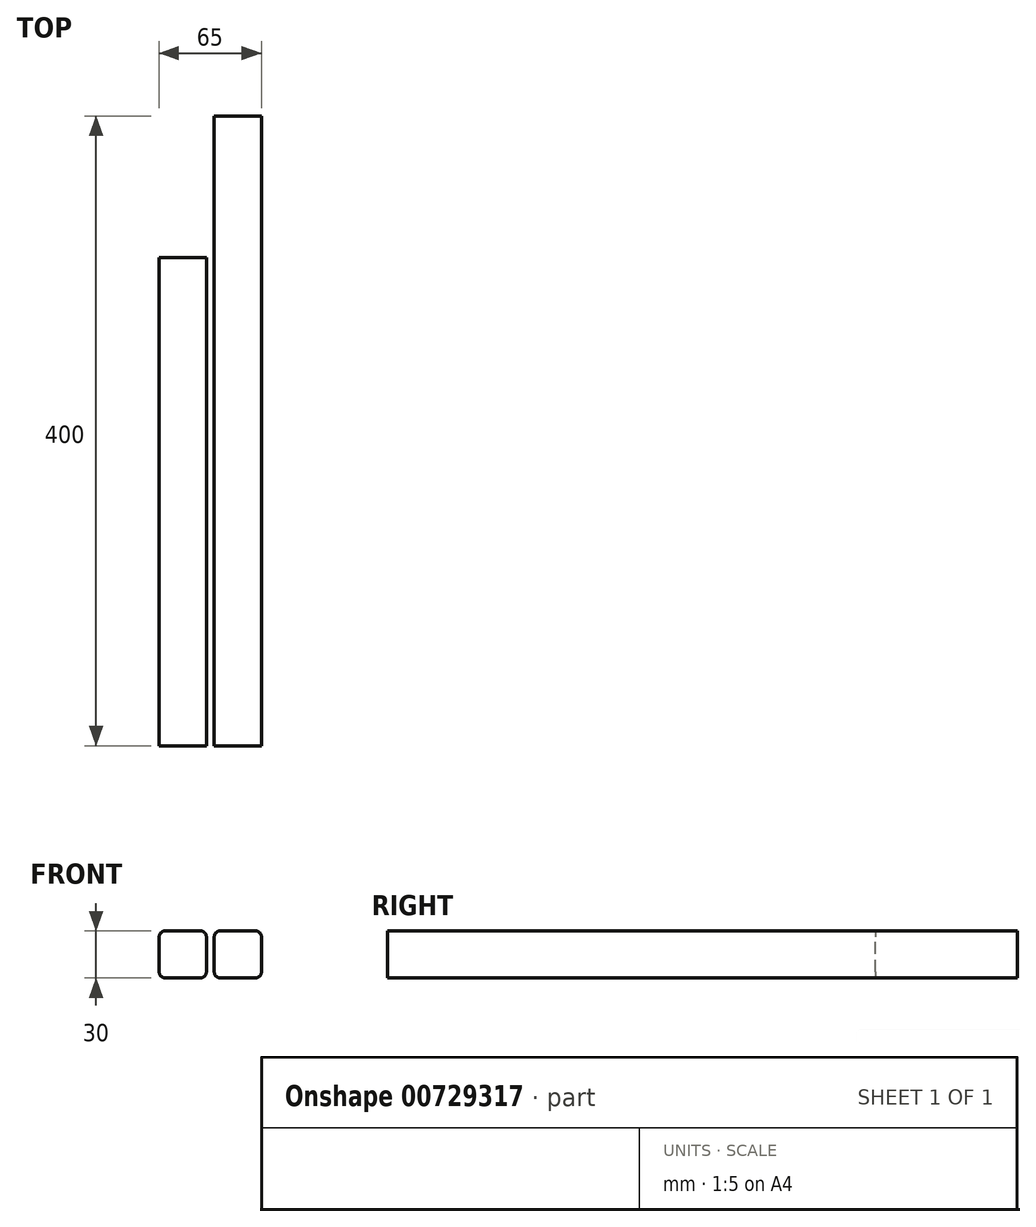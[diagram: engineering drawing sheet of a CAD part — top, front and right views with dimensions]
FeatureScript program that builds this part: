
annotation { "Feature Type Name" : "Feature", "Feature Type Description" : "" }
export const myFeature = defineFeature(function(context is Context, id is Id, definition is map)
    precondition{}
    {
        {
            var Q0;
            Q0=qCreatedBy(makeId("Front.planeOp"),FACE);
            var sketch = newSketch(context, id + "F0", { "sketchPlane" : qUnion([Q0])});
            skLineSegment(sketch, "E0.bottom", {"start": v(0, 0) * mm, "end": v(30, 0) * mm});
            skLineSegment(sketch, "E0.top", {"start": v(0, 30) * mm, "end": v(30, 30) * mm});
            skLineSegment(sketch, "E0.left", {"start": v(0, 0) * mm, "end": v(0, 30) * mm});
            skLineSegment(sketch, "E0.right", {"start": v(30, 0) * mm, "end": v(30, 30) * mm});
            skSolve(sketch);
        }
        {
            var Q0;
            Q0=makeQuery(id+"F0.imprint","IMPRINT",FACE,{"disambiguationData":[TD([[makeQuery(id+"F0.imprint","IMPRINT",EDGE,{"derivedFrom":sQuery(id+"F0.wireOp",EDGE,"E0.bottom")}),1.0]])]});
            extrude(context, id + "F1", {"entities" : qUnion([Q0]), "oppositeDirection" : true, "depth" : 310 * mm, "offsetDistance" : 25 * mm});
        }
        {
            var Q0;
            Q0=makeQuery(id+"F1.opExtrude","SWEPT_EDGE",EDGE,{"disambiguationData":[OSD([sQuery(id+"F0.wireOp",EDGE,"E0.top"),sQuery(id+"F0.wireOp",EDGE,"E0.right")])]});
            var Q1;
            Q1=makeQuery(id+"F1.opExtrude","SWEPT_EDGE",EDGE,{"disambiguationData":[OSD([sQuery(id+"F0.wireOp",EDGE,"E0.bottom"),sQuery(id+"F0.wireOp",EDGE,"E0.right")])]});
            var Q2;
            Q2=makeQuery(id+"F1.opExtrude","SWEPT_EDGE",EDGE,{"disambiguationData":[OSD([sQuery(id+"F0.wireOp",EDGE,"E0.top"),sQuery(id+"F0.wireOp",EDGE,"E0.left")])]});
            var Q3;
            Q3=makeQuery(id+"F1.opExtrude","SWEPT_EDGE",EDGE,{"disambiguationData":[OSD([sQuery(id+"F0.wireOp",EDGE,"E0.bottom"),sQuery(id+"F0.wireOp",EDGE,"E0.left")])]});
            fillet(context, id + "F2", {"entities" : qUnion([Q0, Q1, Q2, Q3]), "radius" : 4 * mm, "tangentPropagation" : true, "defaultsChanged" : true, "vertexSettings" : [], "allowEdgeOverflow" : false});
        }
        {
            var Q0;
            Q0=qCreatedBy(makeId("Front.planeOp"),FACE);
            var sketch = newSketch(context, id + "F3", { "sketchPlane" : qUnion([Q0])});
            skLineSegment(sketch, "E1.bottom", {"start": v(35, 0) * mm, "end": v(65, 0) * mm});
            skLineSegment(sketch, "E1.top", {"start": v(35, 30) * mm, "end": v(65, 30) * mm});
            skLineSegment(sketch, "E1.left", {"start": v(35, 0) * mm, "end": v(35, 30) * mm});
            skLineSegment(sketch, "E1.right", {"start": v(65, 0) * mm, "end": v(65, 30) * mm});
            skSolve(sketch);
        }
        {
            var Q0;
            Q0=makeQuery(id+"F3.imprint","IMPRINT",FACE,{"disambiguationData":[TD([[makeQuery(id+"F3.imprint","IMPRINT",EDGE,{"derivedFrom":sQuery(id+"F3.wireOp",EDGE,"E1.bottom")}),1.0]])]});
            extrude(context, id + "F4", {"entities" : qUnion([Q0]), "oppositeDirection" : true, "depth" : 400 * mm, "offsetDistance" : 25 * mm});
        }
        {
            var Q0;
            Q0=makeQuery(id+"F4.opExtrude","SWEPT_EDGE",EDGE,{"disambiguationData":[OSD([sQuery(id+"F3.wireOp",EDGE,"E1.top"),sQuery(id+"F3.wireOp",EDGE,"E1.left")])]});
            var Q1;
            Q1=makeQuery(id+"F4.opExtrude","SWEPT_EDGE",EDGE,{"disambiguationData":[OSD([sQuery(id+"F3.wireOp",EDGE,"E1.top"),sQuery(id+"F3.wireOp",EDGE,"E1.right")])]});
            var Q2;
            Q2=makeQuery(id+"F4.opExtrude","SWEPT_EDGE",EDGE,{"disambiguationData":[OSD([sQuery(id+"F3.wireOp",EDGE,"E1.bottom"),sQuery(id+"F3.wireOp",EDGE,"E1.right")])]});
            var Q3;
            Q3=makeQuery(id+"F4.opExtrude","SWEPT_EDGE",EDGE,{"disambiguationData":[OSD([sQuery(id+"F3.wireOp",EDGE,"E1.bottom"),sQuery(id+"F3.wireOp",EDGE,"E1.left")])]});
            fillet(context, id + "F5", {"entities" : qUnion([Q0, Q1, Q2, Q3]), "tangentPropagation" : true, "radius" : 4 * mm, "defaultsChanged" : true, "vertexSettings" : [], "allowEdgeOverflow" : false});
        }
    });
